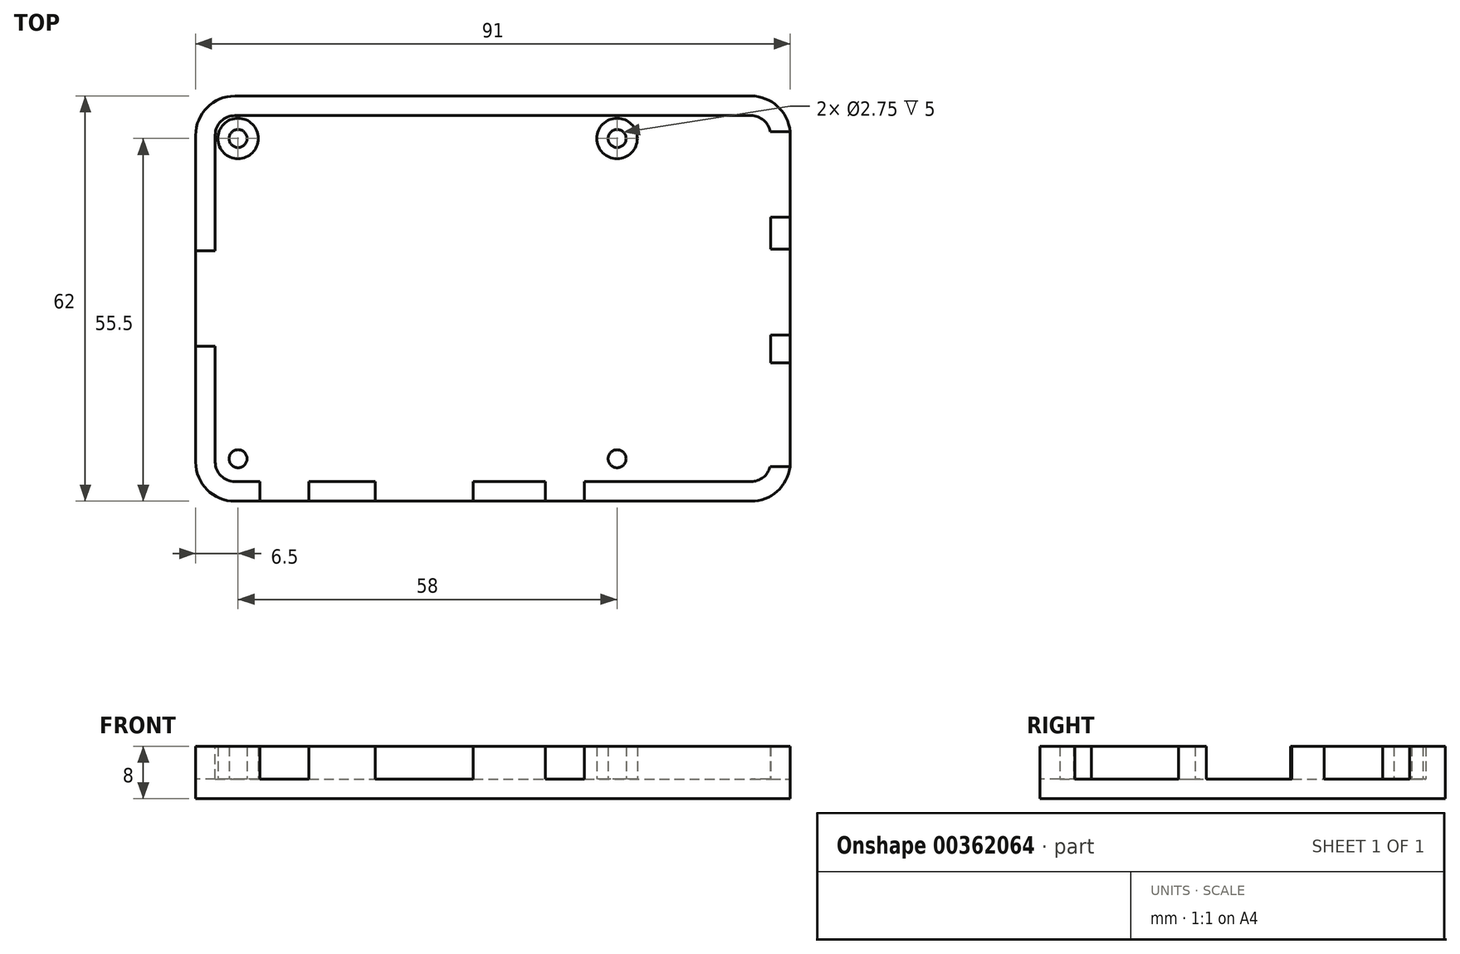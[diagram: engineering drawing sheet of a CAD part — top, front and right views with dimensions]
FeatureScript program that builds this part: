
annotation { "Feature Type Name" : "Feature", "Feature Type Description" : "" }
export const myFeature = defineFeature(function(context is Context, id is Id, definition is map)
    precondition{}
    {
        {
            var Q0;
            Q0=qCreatedBy(makeId("Top.planeOp"),FACE);
            var sketch = newSketch(context, id + "F0", { "sketchPlane" : qUnion([Q0])});
            skLineSegment(sketch, "E0.bottom", {"start": v(3, 0) * mm, "end": v(82, 0) * mm});
            skLineSegment(sketch, "E0.top", {"start": v(3, 56) * mm, "end": v(82, 56) * mm});
            skLineSegment(sketch, "E0.left", {"start": v(0, 3) * mm, "end": v(0, 53) * mm});
            skLineSegment(sketch, "E0.right", {"start": v(85, 3) * mm, "end": v(85, 53) * mm});
            skPoint(sketch, "E1.visualSharp", {"position": v(0, 56) * mm});
            skArc(sketch, "E1.filletArc", {"start": v(3, 56) * mm, "mid": v(0.88, 55.12) * mm, "end": v(0, 53) * mm});
            skPoint(sketch, "E2.visualSharp", {"position": v(0, 0) * mm});
            skArc(sketch, "E2.filletArc", {"start": v(0, 3) * mm, "mid": v(0.88, 0.88) * mm, "end": v(3, 0) * mm});
            skPoint(sketch, "E3.visualSharp", {"position": v(85, 0) * mm});
            skArc(sketch, "E3.filletArc", {"start": v(82, 0) * mm, "mid": v(84.12, 0.88) * mm, "end": v(85, 3) * mm});
            skPoint(sketch, "E4.visualSharp", {"position": v(85, 56) * mm});
            skArc(sketch, "E4.filletArc", {"start": v(85, 53) * mm, "mid": v(84.12, 55.12) * mm, "end": v(82, 56) * mm});
            skCircle(sketch, "E5", {"center": v(3.5, 3.5) * mm, "radius": 3.1 * mm});
            skCircle(sketch, "E6", {"center": v(3.5, 3.5) * mm, "radius": 1.38 * mm});
            skLineSegment(sketch, "E7", {"start": v(0, 28) * mm, "end": v(85, 28) * mm, "construction": true});
            skCircle(sketch, "E8.MirrorC", {"center": v(3.5, 52.5) * mm, "radius": 1.38 * mm});
            skCircle(sketch, "E9.MirrorC", {"center": v(3.5, 52.5) * mm, "radius": 3.1 * mm});
            skCircle(sketch, "E10.1.0.0", {"center": v(61.5, 52.5) * mm, "radius": 1.38 * mm});
            skCircle(sketch, "E10.1.0.1", {"center": v(61.5, 52.5) * mm, "radius": 3.1 * mm});
            skCircle(sketch, "E10.1.0.2", {"center": v(61.5, 3.5) * mm, "radius": 1.38 * mm});
            skCircle(sketch, "E10.1.0.3", {"center": v(61.5, 3.5) * mm, "radius": 3.1 * mm});
            skLineSegment(sketch, "E10.direction1", {"start": v(3.5, 52.5) * mm, "end": v(61.5, 52.5) * mm, "construction": true});
            skArc(sketch, "E11.0", {"start": v(3, 59) * mm, "mid": v(-1.24, 57.24) * mm, "end": v(-3, 53) * mm});
            skLineSegment(sketch, "E11.1", {"start": v(-3, 3) * mm, "end": v(-3, 53) * mm});
            skLineSegment(sketch, "E11.2", {"start": v(3, 59) * mm, "end": v(82, 59) * mm});
            skArc(sketch, "E11.3", {"start": v(-3, 3) * mm, "mid": v(-1.24, -1.24) * mm, "end": v(3, -3) * mm});
            skArc(sketch, "E11.4", {"start": v(88, 53) * mm, "mid": v(86.24, 57.24) * mm, "end": v(82, 59) * mm});
            skLineSegment(sketch, "E11.5", {"start": v(88, 3) * mm, "end": v(88, 53) * mm});
            skArc(sketch, "E11.6", {"start": v(82, -3) * mm, "mid": v(86.24, -1.24) * mm, "end": v(88, 3) * mm});
            skLineSegment(sketch, "E11.7", {"start": v(3, -3) * mm, "end": v(82, -3) * mm});
            skSolve(sketch);
        }
        {
            var Q0;
            Q0=makeQuery(id+"F0.imprint","IMPRINT",FACE,{"disambiguationData":[TD([[makeQuery(id+"F0.imprint","IMPRINT",EDGE,{"derivedFrom":sQuery(id+"F0.wireOp",EDGE,"E0.bottom")}),-1.0]])]});
            extrude(context, id + "F1", {"entities" : qUnion([Q0]), "depth" : 8 * mm});
        }
        {
            var Q0;
            Q0=qSketchRegion(id+"F0",true);
            var Q1;
            Q1=makeQuery(id+"F0.imprint","IMPRINT",FACE,{"disambiguationData":[TD([[makeQuery(id+"F0.imprint","IMPRINT",EDGE,{"derivedFrom":sQuery(id+"F0.wireOp",EDGE,"E0.bottom")}),1.0]])]});
            var Q2;
            Q2=makeQuery(id+"F0.imprint","IMPRINT",FACE,{"disambiguationData":[TD([[makeQuery(id+"F0.imprint","IMPRINT",EDGE,{"derivedFrom":sQuery(id+"F0.wireOp",EDGE,"E5")}),1.0]])]});
            var Q3;
            Q3=makeQuery(id+"F0.imprint","IMPRINT",FACE,{"disambiguationData":[TD([[makeQuery(id+"F0.imprint","IMPRINT",EDGE,{"derivedFrom":sQuery(id+"F0.wireOp",EDGE,"E6")}),1.0]])]});
            var Q4;
            Q4=makeQuery(id+"F0.imprint","IMPRINT",FACE,{"disambiguationData":[TD([[makeQuery(id+"F0.imprint","IMPRINT",EDGE,{"derivedFrom":sQuery(id+"F0.wireOp",EDGE,"E10.1.0.2")}),-1.0]])]});
            var Q5;
            Q5=makeQuery(id+"F0.imprint","IMPRINT",FACE,{"disambiguationData":[TD([[makeQuery(id+"F0.imprint","IMPRINT",EDGE,{"derivedFrom":sQuery(id+"F0.wireOp",EDGE,"E10.1.0.2")}),1.0]])]});
            var Q6;
            Q6=makeQuery(id+"F0.imprint","IMPRINT",FACE,{"disambiguationData":[TD([[makeQuery(id+"F0.imprint","IMPRINT",EDGE,{"derivedFrom":sQuery(id+"F0.wireOp",EDGE,"E10.1.0.0")}),1.0]])]});
            var Q7;
            Q7=makeQuery(id+"F0.imprint","IMPRINT",FACE,{"disambiguationData":[TD([[makeQuery(id+"F0.imprint","IMPRINT",EDGE,{"derivedFrom":sQuery(id+"F0.wireOp",EDGE,"E10.1.0.0")}),-1.0]])]});
            var Q8;
            Q8=makeQuery(id+"F0.imprint","IMPRINT",FACE,{"disambiguationData":[TD([[makeQuery(id+"F0.imprint","IMPRINT",EDGE,{"derivedFrom":sQuery(id+"F0.wireOp",EDGE,"E8.MirrorC")}),1.0]])]});
            var Q9;
            Q9=makeQuery(id+"F0.imprint","IMPRINT",FACE,{"disambiguationData":[TD([[makeQuery(id+"F0.imprint","IMPRINT",EDGE,{"derivedFrom":sQuery(id+"F0.wireOp",EDGE,"E8.MirrorC")}),-1.0]])]});
            extrude(context, id + "F2", {"entities" : qUnion([Q0, Q1, Q2, Q3, Q4, Q5, Q6, Q7, Q8, Q9]), "operationType" : NewBodyOperationType.ADD, "depth" : 3 * mm});
        }
        {
            var Q0;
            Q0=makeQuery(id+"F0.imprint","IMPRINT",FACE,{"disambiguationData":[TD([[makeQuery(id+"F0.imprint","IMPRINT",EDGE,{"derivedFrom":sQuery(id+"F0.wireOp",EDGE,"E6")}),1.0]])]});
            var Q1;
            Q1=makeQuery(id+"F0.imprint","IMPRINT",FACE,{"disambiguationData":[TD([[makeQuery(id+"F0.imprint","IMPRINT",EDGE,{"derivedFrom":sQuery(id+"F0.wireOp",EDGE,"E10.1.0.2")}),1.0]])]});
            var Q2;
            Q2=makeQuery(id+"F0.imprint","IMPRINT",FACE,{"disambiguationData":[TD([[makeQuery(id+"F0.imprint","IMPRINT",EDGE,{"derivedFrom":sQuery(id+"F0.wireOp",EDGE,"E8.MirrorC")}),-1.0]])]});
            var Q3;
            Q3=makeQuery(id+"F0.imprint","IMPRINT",FACE,{"disambiguationData":[TD([[makeQuery(id+"F0.imprint","IMPRINT",EDGE,{"derivedFrom":sQuery(id+"F0.wireOp",EDGE,"E10.1.0.0")}),-1.0]])]});
            extrude(context, id + "F3", {"entities" : qUnion([Q0, Q1, Q2, Q3]), "operationType" : NewBodyOperationType.ADD, "depth" : 8 * mm});
        }
        {
            var Q0;
            Q0=makeQuery(id+"F1.opExtrude","SWEPT_FACE",FACE,{"disambiguationData":[OSD([sQuery(id+"F0.wireOp",EDGE,"E11.7")])]});
            var sketch = newSketch(context, id + "F4", { "sketchPlane" : qUnion([Q0])});
            skLineSegment(sketch, "E12", {"start": v(10.6, 0) * mm, "end": v(10.6, 8) * mm, "construction": true});
            skLineSegment(sketch, "E13.bottom", {"start": v(6.85, 8) * mm, "end": v(14.35, 8) * mm});
            skLineSegment(sketch, "E13.top", {"start": v(6.85, 3) * mm, "end": v(14.35, 3) * mm});
            skLineSegment(sketch, "E13.left", {"start": v(6.85, 8) * mm, "end": v(6.85, 3) * mm});
            skLineSegment(sketch, "E13.right", {"start": v(14.35, 8) * mm, "end": v(14.35, 3) * mm});
            skLineSegment(sketch, "E14", {"start": v(32, 8) * mm, "end": v(32, 0) * mm, "construction": true});
            skLineSegment(sketch, "E15.bottom", {"start": v(24.5, 8) * mm, "end": v(39.5, 8) * mm});
            skLineSegment(sketch, "E15.top", {"start": v(24.5, 3) * mm, "end": v(39.5, 3) * mm});
            skLineSegment(sketch, "E15.left", {"start": v(24.5, 8) * mm, "end": v(24.5, 3) * mm});
            skLineSegment(sketch, "E15.right", {"start": v(39.5, 8) * mm, "end": v(39.5, 3) * mm});
            skLineSegment(sketch, "E16", {"start": v(53.5, 8) * mm, "end": v(53.5, 0) * mm, "construction": true});
            skLineSegment(sketch, "E17.bottom", {"start": v(50.5, 8) * mm, "end": v(56.5, 8) * mm});
            skLineSegment(sketch, "E17.top", {"start": v(50.5, 3) * mm, "end": v(56.5, 3) * mm});
            skLineSegment(sketch, "E17.left", {"start": v(50.5, 8) * mm, "end": v(50.5, 3) * mm});
            skLineSegment(sketch, "E17.right", {"start": v(56.5, 8) * mm, "end": v(56.5, 3) * mm});
            skSolve(sketch);
        }
        {
            var Q0;
            Q0=makeQuery(id+"F4.imprint","IMPRINT",FACE,{"disambiguationData":[TD([[makeQuery(id+"F4.imprint","IMPRINT",EDGE,{"derivedFrom":sQuery(id+"F4.wireOp",EDGE,"E13.bottom")}),-1.0]])]});
            var Q1;
            Q1=makeQuery(id+"F1.opExtrude","SWEPT_FACE",FACE,{"disambiguationData":[OSD([sQuery(id+"F0.wireOp",EDGE,"E0.bottom")])]});
            extrude(context, id + "F5", {"entities" : qUnion([Q0]), "operationType" : NewBodyOperationType.REMOVE, "endBound" : BoundingType.UP_TO_SURFACE, "oppositeDirection" : true, "endBoundEntityFace" : qUnion([Q1]), "depth" : 25 * mm});
        }
        {
            var Q0;
            Q0=qSketchRegion(id+"F4",true);
            var Q1;
            {var subQ8=sQuery(id+"F0.wireOp",EDGE,"E3.filletArc");var subQ9=sQuery(id+"F0.wireOp",EDGE,"E0.bottom");Q1=makeQuery(id+"F5.boolean.opBoolean","SPLIT",FACE,{"disambiguationData":[TD([makeQuery(id+"F1.opExtrude","SWEPT_FACE",FACE,{"disambiguationData":[OSD([subQ8])]})])],"derivedFrom":makeQuery(id+"F1.opExtrude","SWEPT_FACE",FACE,{"disambiguationData":[OSD([subQ9])]})});}
            extrude(context, id + "F6", {"entities" : qUnion([Q0]), "operationType" : NewBodyOperationType.REMOVE, "endBound" : BoundingType.UP_TO_SURFACE, "oppositeDirection" : true, "endBoundEntityFace" : qUnion([Q1]), "depth" : 25 * mm});
        }
        {
            var Q0;
            Q0=makeQuery(id+"F1.opExtrude","SWEPT_FACE",FACE,{"disambiguationData":[OSD([sQuery(id+"F0.wireOp",EDGE,"E11.5")])]});
            var sketch = newSketch(context, id + "F7", { "sketchPlane" : qUnion([Q0])});
            skLineSegment(sketch, "E18", {"start": v(10.25, 8) * mm, "end": v(10.25, 0) * mm, "construction": true});
            skLineSegment(sketch, "E19", {"start": v(29, 8) * mm, "end": v(29, 0) * mm, "construction": true});
            skLineSegment(sketch, "E20", {"start": v(47, 8) * mm, "end": v(47, 0) * mm, "construction": true});
            skLineSegment(sketch, "E21.bottom", {"start": v(2.3, 8) * mm, "end": v(18.2, 8) * mm});
            skLineSegment(sketch, "E21.top", {"start": v(2.3, 3) * mm, "end": v(18.2, 3) * mm});
            skLineSegment(sketch, "E21.left", {"start": v(2.3, 8) * mm, "end": v(2.3, 3) * mm});
            skLineSegment(sketch, "E21.right", {"start": v(18.2, 8) * mm, "end": v(18.2, 3) * mm});
            skLineSegment(sketch, "E22.bottom", {"start": v(22.45, 8) * mm, "end": v(35.55, 8) * mm});
            skLineSegment(sketch, "E22.top", {"start": v(22.45, 3) * mm, "end": v(35.55, 3) * mm});
            skLineSegment(sketch, "E22.left", {"start": v(22.45, 8) * mm, "end": v(22.45, 3) * mm});
            skLineSegment(sketch, "E22.right", {"start": v(35.55, 8) * mm, "end": v(35.55, 3) * mm});
            skLineSegment(sketch, "E23.bottom", {"start": v(40.45, 8) * mm, "end": v(53.55, 8) * mm});
            skLineSegment(sketch, "E23.top", {"start": v(40.45, 3) * mm, "end": v(53.55, 3) * mm});
            skLineSegment(sketch, "E23.left", {"start": v(40.45, 8) * mm, "end": v(40.45, 3) * mm});
            skLineSegment(sketch, "E23.right", {"start": v(53.55, 8) * mm, "end": v(53.55, 3) * mm});
            skSolve(sketch);
        }
        {
            var Q0;
            Q0=qSketchRegion(id+"F7",true);
            var Q1;
            Q1=makeQuery(id+"F1.opExtrude","SWEPT_FACE",FACE,{"disambiguationData":[OSD([sQuery(id+"F0.wireOp",EDGE,"E0.right")])]});
            extrude(context, id + "F8", {"entities" : qUnion([Q0]), "operationType" : NewBodyOperationType.REMOVE, "endBound" : BoundingType.UP_TO_SURFACE, "oppositeDirection" : true, "endBoundEntityFace" : qUnion([Q1]), "depth" : 25 * mm});
        }
        {
            var Q0;
            Q0=makeQuery(id+"F1.opExtrude","SWEPT_FACE",FACE,{"disambiguationData":[OSD([sQuery(id+"F0.wireOp",EDGE,"E11.1")])]});
            var sketch = newSketch(context, id + "F9", { "sketchPlane" : qUnion([Q0])});
            skLineSegment(sketch, "E24", {"start": v(-28, 0) * mm, "end": v(-28, 8) * mm, "construction": true});
            skLineSegment(sketch, "E25.bottom", {"start": v(-35.3, 8) * mm, "end": v(-20.7, 8) * mm});
            skLineSegment(sketch, "E25.top", {"start": v(-35.3, 3) * mm, "end": v(-20.7, 3) * mm});
            skLineSegment(sketch, "E25.left", {"start": v(-35.3, 8) * mm, "end": v(-35.3, 3) * mm});
            skLineSegment(sketch, "E25.right", {"start": v(-20.7, 8) * mm, "end": v(-20.7, 3) * mm});
            skSolve(sketch);
        }
        {
            var Q0;
            Q0=qSketchRegion(id+"F9",true);
            var Q1;
            Q1=makeQuery(id+"F1.opExtrude","SWEPT_FACE",FACE,{"disambiguationData":[OSD([sQuery(id+"F0.wireOp",EDGE,"E0.left")])]});
            extrude(context, id + "F10", {"entities" : qUnion([Q0]), "operationType" : NewBodyOperationType.REMOVE, "endBound" : BoundingType.UP_TO_SURFACE, "oppositeDirection" : true, "endBoundEntityFace" : qUnion([Q1]), "depth" : 25 * mm});
        }
        {
            var Q0;
            Q0=qSketchRegion(id+"F7",true);
            extrude(context, id + "F11", {"entities" : qUnion([Q0]), "operationType" : NewBodyOperationType.REMOVE, "oppositeDirection" : true, "depth" : 10 * mm});
        }
    });
